FCSTD DOCUMENT
Label: divider A
objects: Sketcher::SketchObject×1
note: 1 computed .brp shape members not serialized (recipe doc carries the construction recipe); baked Part::Feature solids carry a one-line shape summary decoded from their .brp

FEATURE [Sketcher::SketchObject] Sketch  label="divider A"
  sketch-geometry (20):
    g0: LineSegment StartX=0.198153 StartY=34.5 StartZ=0 EndX=29.1982 EndY=34.5 EndZ=0
    g1: LineSegment StartX=29.1982 StartY=34.5 StartZ=0 EndX=29.1982 EndY=17.25 EndZ=0
    g2: LineSegment StartX=29.1982 StartY=17.25 StartZ=0 EndX=32.1982 EndY=17.25 EndZ=0
    g3: LineSegment StartX=32.1982 StartY=17.25 StartZ=0 EndX=32.1982 EndY=34.5 EndZ=0
    g4: LineSegment StartX=32.1982 StartY=34.5 StartZ=0 EndX=61.1982 EndY=34.5 EndZ=0
    g5: LineSegment StartX=61.1982 StartY=34.5 StartZ=0 EndX=61.1982 EndY=17.25 EndZ=0
    g6: LineSegment StartX=61.1982 StartY=17.25 StartZ=0 EndX=64.1982 EndY=17.25 EndZ=0
    g7: LineSegment StartX=64.1982 StartY=17.25 StartZ=0 EndX=64.1982 EndY=34.5 EndZ=0
    g8: LineSegment StartX=64.1982 StartY=34.5 StartZ=0 EndX=93.1982 EndY=34.5 EndZ=0
    g9: LineSegment StartX=93.1982 StartY=34.5 StartZ=0 EndX=93.1982 EndY=17.25 EndZ=0
    g10: LineSegment StartX=93.1982 StartY=17.25 StartZ=0 EndX=96.1982 EndY=17.25 EndZ=0
    g11: LineSegment StartX=96.1982 StartY=17.25 StartZ=0 EndX=96.1982 EndY=34.5 EndZ=0
    g12: LineSegment StartX=96.1982 StartY=34.5 StartZ=0 EndX=125.198 EndY=34.5 EndZ=0
    g13: LineSegment StartX=125.198 StartY=34.5 StartZ=0 EndX=125.198 EndY=17.25 EndZ=0
    g14: LineSegment StartX=125.198 StartY=17.25 StartZ=0 EndX=122.198 EndY=17.25 EndZ=0
    g15: LineSegment StartX=122.198 StartY=17.25 StartZ=0 EndX=122.198 EndY=0 EndZ=0
    g16: LineSegment StartX=122.198 StartY=0 StartZ=0 EndX=3.19815 EndY=0 EndZ=0
    g17: LineSegment StartX=3.19815 StartY=0 StartZ=0 EndX=3.19815 EndY=17.25 EndZ=0
    g18: LineSegment StartX=3.19815 StartY=17.25 StartZ=0 EndX=0.198153 EndY=17.25 EndZ=0
    g19: LineSegment StartX=0.198153 StartY=17.25 StartZ=0 EndX=0.198153 EndY=34.5 EndZ=0
  constraints (60):
    c: Horizontal(g0)
    c: Coincident(g0,g1)
    c: Vertical(g1)
    c: Coincident(g1,g2)
    c: Horizontal(g2)
    c: Coincident(g2,g3)
    c: Coincident(g3,g4)
    c: Horizontal(g4)
    c: Coincident(g4,g5)
    c: Coincident(g5,g6)
    c: Horizontal(g6)
    c: Coincident(g6,g7)
    c: Coincident(g7,g8)
    c: Coincident(g8,g9)
    c: Vertical(g9)
    c: Coincident(g9,g10)
    c: Coincident(g10,g11)
    c: Vertical(g11)
    c: Coincident(g11,g12)
    c: Horizontal(g12)
    c: Coincident(g12,g13)
    c: Vertical(g13)
    c: Coincident(g13,g14)
    c: Coincident(g14,g15)
    c: Vertical(g15)
    c: Coincident(g15,g16)
    c: Horizontal(g16)
    c: Coincident(g16,g17)
    c: Vertical(g17)
    c: Coincident(g17,g18)
    c: Coincident(g18,g19)
    c: Coincident(g19,g0)
    c: Horizontal(g10)
    c: Horizontal(g14)
    c: Horizontal(g18)
    c: Vertical(g19)
    c: Vertical(g3)
    c: Vertical(g5)
    c: Vertical(g7)
    c: Horizontal(g8)
    c: DistanceY(g0,g3) = 0
    c: DistanceY(g4,g7) = 0
    c: DistanceY(g8,g11) = 0
    c: DistanceY(g6,g9) = 0
    c: DistanceY(g5,g2) = 0
    c: DistanceX(g1,g2) = 3
    c: DistanceX(g5,g6) = 3
    c: DistanceX(g8,g11) = 3
    c: DistanceY(g15,g12) = 34.5
    c: DistanceY(g13,g12) = 17.25
    c: DistanceY(g10,g14) = 0
    c: DistanceY(g17,g1) = 0
    c: DistanceX(g13,g14) = -3
    c: DistanceX(g18,g17) = 3
    c: DistanceX(g12,g11) = -29
    c: DistanceX(g4,g3) = -29
    c: DistanceX(g0,g0) = -29
    c: DistanceX(g7,g8) = 29
    c: DistanceX(g16) = 3.19815
    c: DistanceY(g16) = 0
